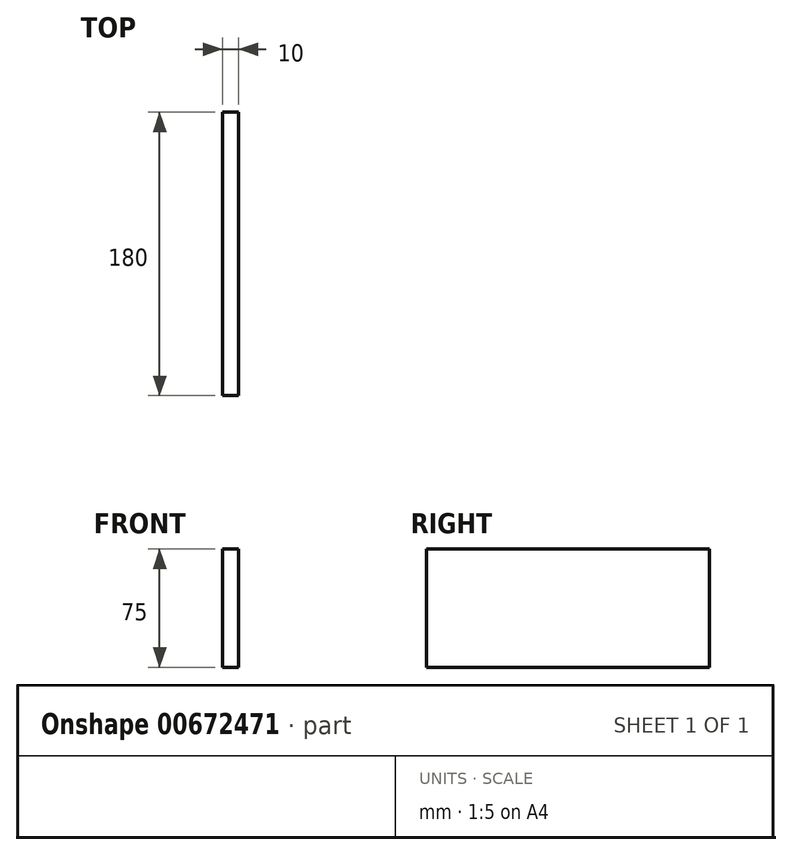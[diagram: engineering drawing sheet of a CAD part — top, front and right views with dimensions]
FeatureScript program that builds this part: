
annotation { "Feature Type Name" : "Feature", "Feature Type Description" : "" }
export const myFeature = defineFeature(function(context is Context, id is Id, definition is map)
    precondition{}
    {
        {
            var Q0;
            Q0=qCreatedBy(makeId("Right.planeOp"),FACE);
            var sketch = newSketch(context, id + "F0", { "sketchPlane" : qUnion([Q0])});
            skLineSegment(sketch, "E0.bottom", {"start": v(90, -37.5) * mm, "end": v(-90, -37.5) * mm});
            skLineSegment(sketch, "E0.top", {"start": v(90, 37.5) * mm, "end": v(-90, 37.5) * mm});
            skLineSegment(sketch, "E0.left", {"start": v(90, -37.5) * mm, "end": v(90, 37.5) * mm});
            skLineSegment(sketch, "E0.right", {"start": v(-90, -37.5) * mm, "end": v(-90, 37.5) * mm});
            skPoint(sketch, "E0.middle", {"position": v(0, 0) * mm});
            skSolve(sketch);
        }
        {
            var Q0;
            Q0=qSketchRegion(id+"F0",true);
            extrude(context, id + "F1", {"entities" : qUnion([Q0]), "depth" : 10 * mm, "offsetDistance" : 25 * mm});
        }
    });
